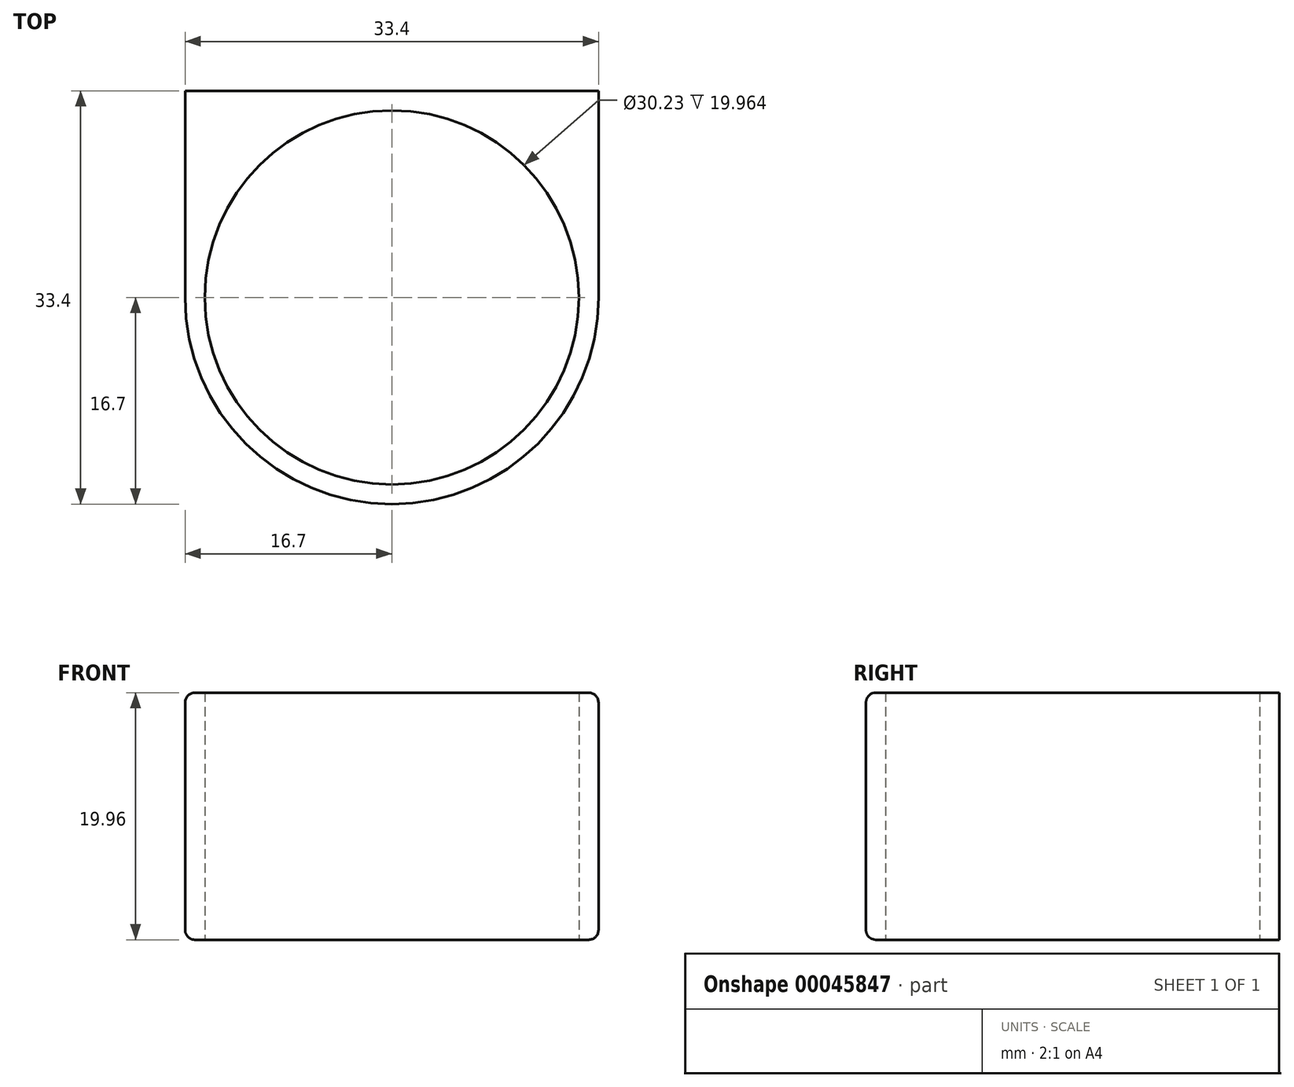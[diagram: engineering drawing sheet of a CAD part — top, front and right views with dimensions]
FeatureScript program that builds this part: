
annotation { "Feature Type Name" : "Feature", "Feature Type Description" : "" }
export const myFeature = defineFeature(function(context is Context, id is Id, definition is map)
    precondition{}
    {
        {
            var Q0;
            Q0=qCreatedBy(makeId("Top.planeOp"),FACE);
            var sketch = newSketch(context, id + "F0", { "sketchPlane" : qUnion([Q0])});
            skCircle(sketch, "E0", {"center": v(0, 0) * mm, "radius": 15.11 * mm});
            skLineSegment(sketch, "E1.rect.bottom", {"start": v(16.7, 16.7) * mm, "end": v(-16.7, 16.7) * mm});
            skLineSegment(sketch, "E1.rect.top", {"start": v(16.7, -16.7) * mm, "end": v(-16.7, -16.7) * mm});
            skLineSegment(sketch, "E1.rect.left", {"start": v(16.7, 16.7) * mm, "end": v(16.7, -16.7) * mm});
            skLineSegment(sketch, "E1.rect.right", {"start": v(-16.7, 16.7) * mm, "end": v(-16.7, -16.7) * mm});
            skSolve(sketch);
        }
        {
            var Q0;
            Q0=qSketchRegion(id+"F0",true);
            extrude(context, id + "F1", {"entities" : qUnion([Q0]), "depth" : 19.96 * mm});
        }
        {
            var Q0;
            Q0=makeQuery(id+"F1.opExtrude","SWEPT_EDGE",EDGE,{"disambiguationData":[OSD([sQuery(id+"F0.wireOp",EDGE,"E1.rect.top"),sQuery(id+"F0.wireOp",EDGE,"E1.rect.right")])]});
            var Q1;
            Q1=makeQuery(id+"F1.opExtrude","SWEPT_EDGE",EDGE,{"disambiguationData":[OSD([sQuery(id+"F0.wireOp",EDGE,"E1.rect.top"),sQuery(id+"F0.wireOp",EDGE,"E1.rect.left")])]});
            fillet(context, id + "F2", {"entities" : qUnion([Q0, Q1]), "radius" : 16.7 * mm, "tangentPropagation" : true, "allowEdgeOverflow" : false});
        }
        {
            var Q0;
            {var subQ0=sQuery(id+"F0.wireOp",EDGE,"E1.rect.top");var subQ1=sQuery(id+"F0.wireOp",EDGE,"E1.rect.left");Q0=makeQuery(id+"F2.opFillet","BLEND_EDGE",EDGE,{"blendedFrom":[makeQuery(id+"F1.opExtrude","SWEPT_EDGE",EDGE,{"disambiguationData":[OSD([subQ0,subQ1])]}),makeQuery(id+"F1.opExtrude","CAP_FACE",FACE,{"disambiguationData":[OSD([sQuery(id+"F0.wireOp",EDGE,"E0"),sQuery(id+"F0.wireOp",EDGE,"E1.rect.bottom"),subQ0,subQ1,sQuery(id+"F0.wireOp",EDGE,"E1.rect.right")])],"isStart":false})],"blendedInto":[makeQuery(id+"F1.opExtrude","CAP_FACE",FACE,{"disambiguationData":[OSD([sQuery(id+"F0.wireOp",EDGE,"E0"),sQuery(id+"F0.wireOp",EDGE,"E1.rect.bottom"),subQ0,subQ1,sQuery(id+"F0.wireOp",EDGE,"E1.rect.right")])],"isStart":false})]});}
            var Q1;
            {var subQ0=sQuery(id+"F0.wireOp",EDGE,"E1.rect.top");var subQ1=sQuery(id+"F0.wireOp",EDGE,"E1.rect.left");Q1=makeQuery(id+"F2.opFillet","BLEND_EDGE",EDGE,{"blendedFrom":[makeQuery(id+"F1.opExtrude","SWEPT_EDGE",EDGE,{"disambiguationData":[OSD([subQ0,subQ1])]}),makeQuery(id+"F1.opExtrude","CAP_FACE",FACE,{"disambiguationData":[OSD([sQuery(id+"F0.wireOp",EDGE,"E0"),sQuery(id+"F0.wireOp",EDGE,"E1.rect.bottom"),subQ0,subQ1,sQuery(id+"F0.wireOp",EDGE,"E1.rect.right")])],"isStart":true})],"blendedInto":[makeQuery(id+"F1.opExtrude","CAP_FACE",FACE,{"disambiguationData":[OSD([sQuery(id+"F0.wireOp",EDGE,"E0"),sQuery(id+"F0.wireOp",EDGE,"E1.rect.bottom"),subQ0,subQ1,sQuery(id+"F0.wireOp",EDGE,"E1.rect.right")])],"isStart":true})]});}
            fillet(context, id + "F3", {"entities" : qUnion([Q0, Q1]), "radius" : 0.8 * mm, "tangentPropagation" : true, "allowEdgeOverflow" : false});
        }
    });
